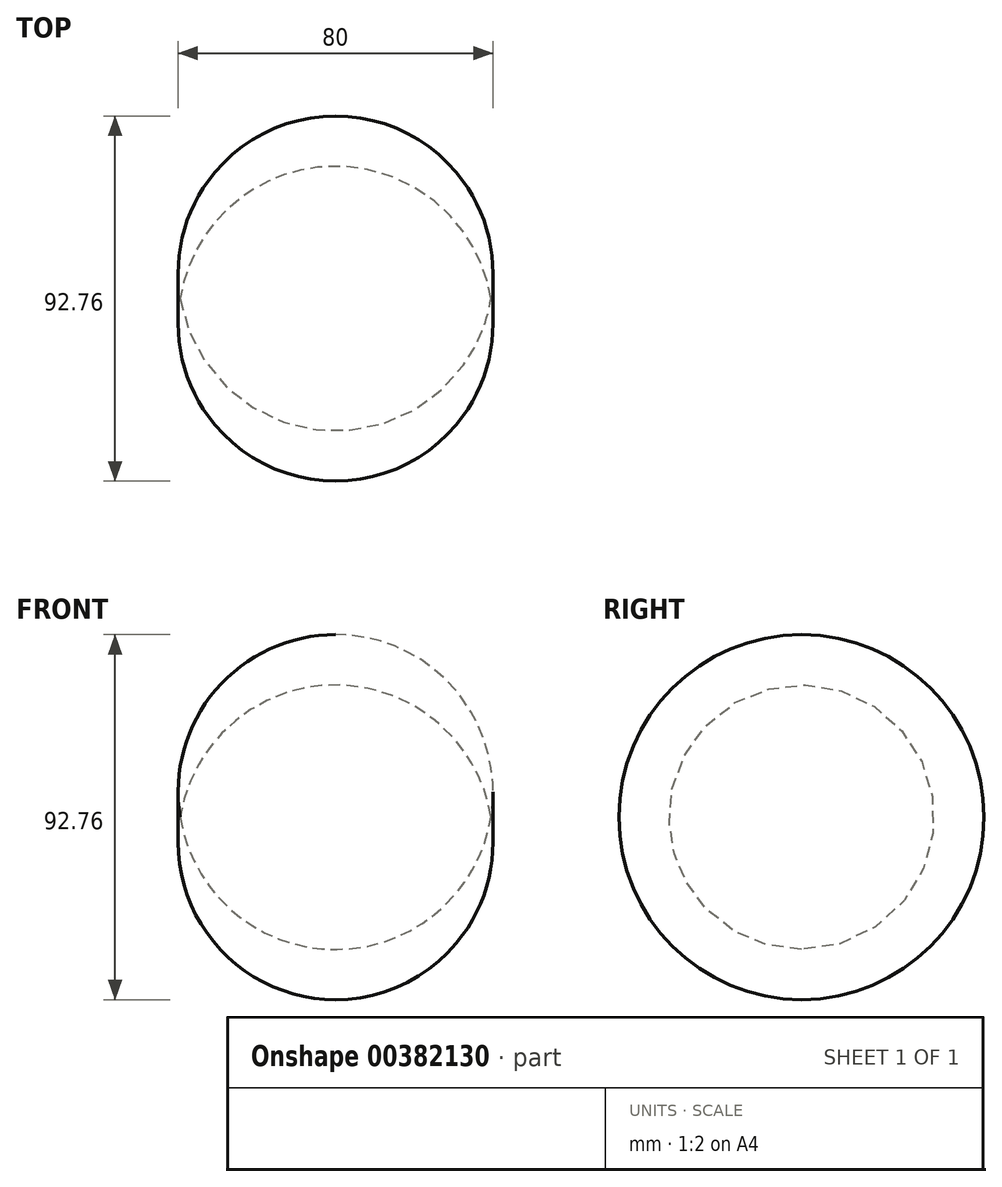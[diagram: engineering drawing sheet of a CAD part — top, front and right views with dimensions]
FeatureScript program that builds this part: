
annotation { "Feature Type Name" : "Feature", "Feature Type Description" : "" }
export const myFeature = defineFeature(function(context is Context, id is Id, definition is map)
    precondition{}
    {
        {
            var Q0;
            Q0=qCreatedBy(makeId("Front.planeOp"),FACE);
            var sketch = newSketch(context, id + "F0", { "sketchPlane" : qUnion([Q0])});
            skLineSegment(sketch, "E0", {"start": v(-46.44, 0) * mm, "end": v(50.42, 0) * mm, "construction": true});
            skArc(sketch, "E1", {"start": v(39.02, 0) * mm, "mid": v(-0.46, 33.62) * mm, "end": v(-39.95, 0) * mm});
            skLineSegment(sketch, "E2", {"start": v(-39.95, 0) * mm, "end": v(39.02, 0) * mm});
            skSolve(sketch);
        }
        {
            var Q0;
            Q0 = qSketchRegion(id + "F0", true);
            var Q1;
            Q1=sQuery(id+"F0.wireOp",EDGE,"E0");
            revolve(context, id + "F1", {"entities" : qUnion([Q0]), "axis" : qUnion([Q1]), "revolveType" : RevolveType.FULL});
        }
    });
